# Revit family: RTD-CB_Back-Flow_DN15-25_RFA
name_source: partatom
category: Pipe Accessories
units: mm (PartAtom-declared; Revit-internal decimal feet)

## family parameters
Always vertical = Yes
Cut with Voids When Loaded = No
OmniClass Number = 23.65.55.14.17
OmniClass Title = Adjusting/Controlling Valves for Liquid Services
Part Type = Valve - Breaks Into
Round Connector Dimension = Use Diameter
Shared = No
Work Plane-Based = No

## types (2) — shared parameters
Description = Flow Restrictor
IfcExportAs = IfcValveType
IfcExportType = RTD-CB
L1_1 = 18 mm  [stored 0.0590551 ft]
LOD 200 = No
LOD 350 = Yes
Manufacturer = Danfoss
Max Operating Pressure = 10 bar
Max Working Temperature = 120 °C
URL = https://store.danfoss.com
Valve Body Material = Danfoss Stainless Steel AISI 304 / AISI 316L

## per-type parameters (varying)
| type | D | D1 | H | H1 | Kvs | L1 | L2 | L3 | LL | Model | Model Type | R1 | R_200 | R_200_1 | S1 | S2 | S3 | TL |
| RTD-CB_Back-Flow_DN20_013L1926 | 20 mm  [stored 0.0656168 ft] | 26 mm | 48 mm  [stored 0.15748 ft] | 24 mm  [stored 0.0787402 ft] | 8.1 m³/h | 12 mm  [stored 0.0393701 ft] | 17 mm | 22 mm  [stored 0.0721785 ft] | 55 mm  [stored 0.180446 ft] | 013L1926 | RTD-CB_Back-Flow_DN20 | 12 mm  [stored 0.0393701 ft] | 18 mm  [stored 0.0590551 ft] | 20 mm  [stored 0.0656168 ft] | 16 mm  [stored 0.0524934 ft] | 32 mm  [stored 0.104987 ft] | 37 mm  [stored 0.121391 ft] | 53 mm  [stored 0.173885 ft] |
| RTD-CB_Back-Flow_DN15_013L1925 | 15 mm  [stored 0.0492126 ft] | 24 mm  [stored 0.0787402 ft] | 32 mm  [stored 0.104987 ft] | 11 mm  [stored 0.0360892 ft] | 4.5 m³/h | 11 mm  [stored 0.0360892 ft] | 16 mm  [stored 0.0524934 ft] | 20 mm  [stored 0.0656168 ft] | 50 mm | 013L1925 | RTD-CB_Back-Flow_DN15 | 10 mm  [stored 0.0328084 ft] | 15 mm  [stored 0.0492126 ft] | 16 mm  [stored 0.0524934 ft] | 14 mm  [stored 0.0459318 ft] | 27 mm  [stored 0.0885827 ft] | 30 mm  [stored 0.0984252 ft] | 48 mm  [stored 0.15748 ft] |

note: [stored X ft] marks values corroborated as IEEE doubles in the binary element streams (Revit-internal decimal feet)

## geometry (parser evidence)
native form markers: Sweep x3
no freeform markers — native parametric forms only
